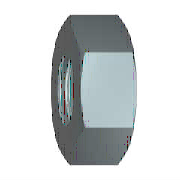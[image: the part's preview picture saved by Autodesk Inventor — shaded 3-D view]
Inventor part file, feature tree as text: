
AUTODESK INVENTOR PART (.ipt)
format: ipt  version: 2015 (Build 190159000, 159)  size: 162,304 bytes
history: native  units: mm (DEFAULTED — no unit token found)
features: sketch x3, other x2, extrude x1, hole x1, plane x1
ambient origin geometry x7: Origin, YZ Plane, XZ Plane, X Axis, Y Axis, Z Axis, Center Point
bodies: Body1 (feature_tree)
feature tree (8):
  extrude  "Bryła"  Depth=15.011107mm
  other  "Faza1"
  hole  "Gwint"  [1 undecoded]
  other  "Work Axis1"
  plane  "Work Plane1"
  sketch  "Szkic1"
  sketch  "Szkic2"
  sketch  "Szkic3"
note: 1 required parameter value undecoded (feature->parameter linkage not recoverable at this tier; creation-order binding heuristic only, values carry confidence <= 0.55)
